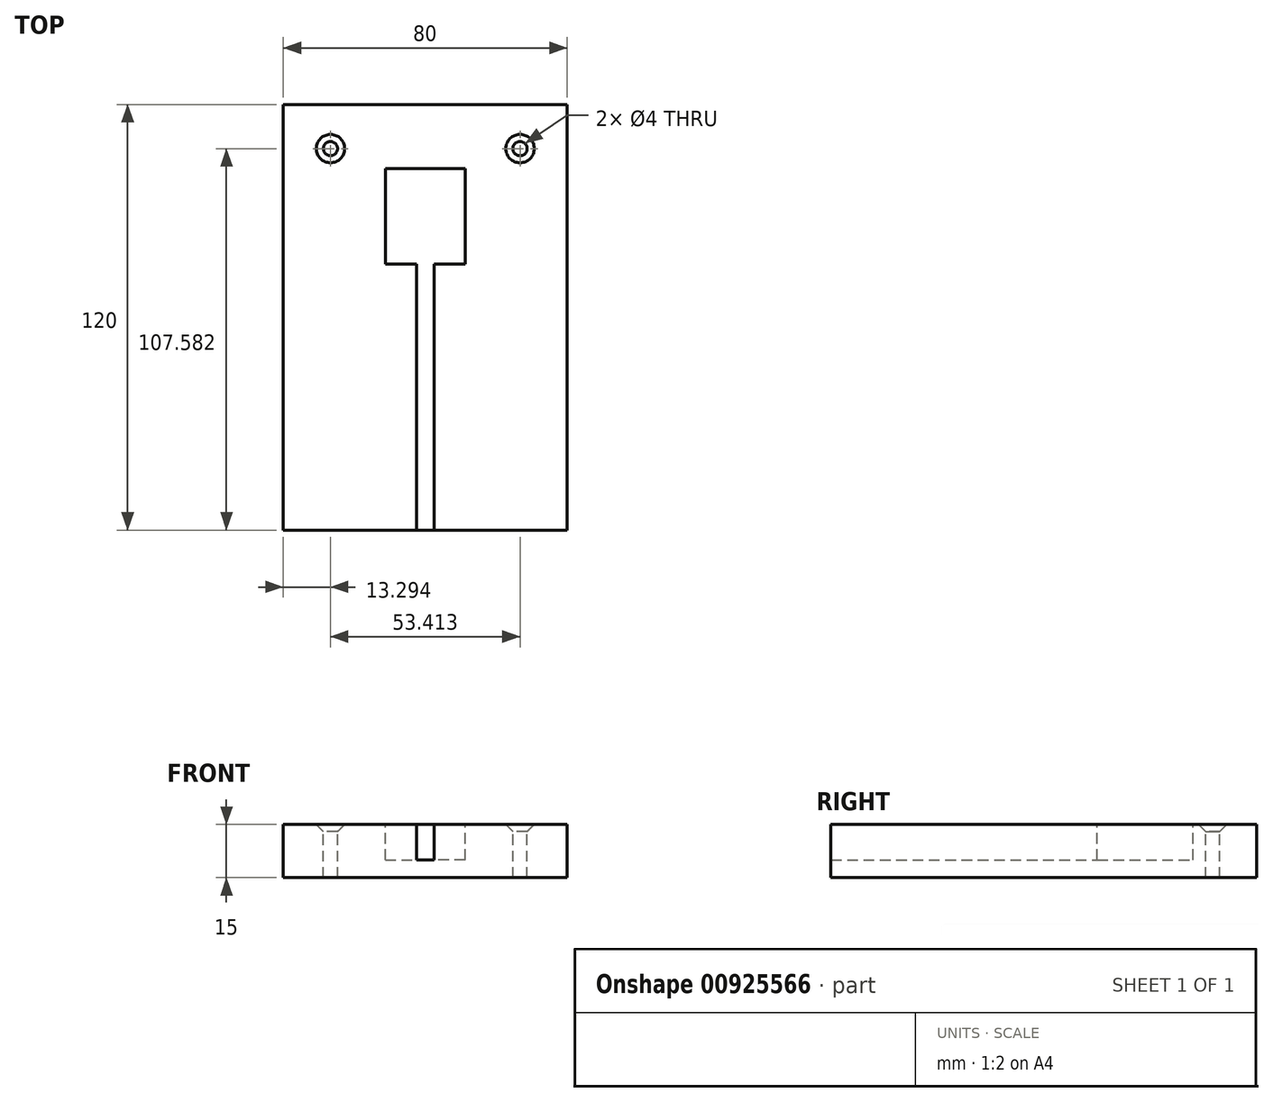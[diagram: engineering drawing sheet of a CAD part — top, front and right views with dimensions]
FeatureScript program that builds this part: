
annotation { "Feature Type Name" : "Feature", "Feature Type Description" : "" }
export const myFeature = defineFeature(function(context is Context, id is Id, definition is map)
    precondition{}
    {
        {
            var Q0;
            Q0=qCreatedBy(makeId("Top.planeOp"),FACE);
            var sketch = newSketch(context, id + "F0", { "sketchPlane" : qUnion([Q0])});
            skLineSegment(sketch, "E0.bottom", {"start": v(-40, 60) * mm, "end": v(40, 60) * mm});
            skLineSegment(sketch, "E0.top", {"start": v(-40, -60) * mm, "end": v(40, -60) * mm});
            skLineSegment(sketch, "E0.left", {"start": v(-40, 60) * mm, "end": v(-40, -60) * mm});
            skLineSegment(sketch, "E0.right", {"start": v(40, 60) * mm, "end": v(40, -60) * mm});
            skPoint(sketch, "E0.middle", {"position": v(0, 0) * mm});
            skSolve(sketch);
        }
        {
            var Q0;
            Q0 = qSketchRegion(id + "F0", true);
            extrude(context, id + "F1", {"entities" : qUnion([Q0]), "depth" : 15 * mm, "offsetDistance" : 25 * mm});
        }
        {
            var Q0;
            Q0=makeQuery(id+"F1.opExtrude","CAP_FACE",FACE,{"disambiguationData":[OSD([sQuery(id+"F0.wireOp",EDGE,"E0.bottom"),sQuery(id+"F0.wireOp",EDGE,"E0.top"),sQuery(id+"F0.wireOp",EDGE,"E0.left"),sQuery(id+"F0.wireOp",EDGE,"E0.right")])],"isStart":false});
            var sketch = newSketch(context, id + "F2", { "sketchPlane" : qUnion([Q0])});
            skLineSegment(sketch, "E1", {"start": v(-2.5, 15) * mm, "end": v(-11.26, 15) * mm});
            skLineSegment(sketch, "E2", {"start": v(-11.26, 15) * mm, "end": v(-11.26, 42) * mm});
            skLineSegment(sketch, "E3", {"start": v(0, -60) * mm, "end": v(-2.5, -60) * mm});
            skLineSegment(sketch, "E4", {"start": v(-2.5, -60) * mm, "end": v(-2.5, 15) * mm});
            skLineSegment(sketch, "E5.MirrorCS", {"start": v(2.5, -60) * mm, "end": v(2.5, 15) * mm});
            skPoint(sketch, "E6.end.orphan", {"position": v(0, 15) * mm});
            skPoint(sketch, "E7.end.orphan", {"position": v(6.37, 15) * mm});
            skPoint(sketch, "E8.start.orphan", {"position": v(0, 42) * mm});
            skPoint(sketch, "E9.end.orphan", {"position": v(12.75, 15) * mm});
            skLineSegment(sketch, "E10", {"start": v(0, 60) * mm, "end": v(0, 50.46) * mm});
            skLineSegment(sketch, "E11.MirrorCS", {"start": v(11.26, 15) * mm, "end": v(11.26, 42) * mm});
            skLineSegment(sketch, "E12", {"start": v(-11.26, 42) * mm, "end": v(11.26, 42) * mm});
            skLineSegment(sketch, "E13", {"start": v(11.26, 15) * mm, "end": v(2.5, 15) * mm});
            skSolve(sketch);
        }
        {
            var Q0;
            Q0 = qSketchRegion(id + "F2", true);
            var Q1;
            Q1=makeQuery(id+"F2.imprint","IMPRINT",FACE,{"disambiguationData":[TD([[makeQuery(id+"F2.imprint","IMPRINT",EDGE,{"derivedFrom":sQuery(id+"F2.wireOp",EDGE,"E1")}),-1.0]])]});
            extrude(context, id + "F3", {"entities" : qUnion([Q0, Q1]), "operationType" : NewBodyOperationType.REMOVE, "oppositeDirection" : true, "depth" : 10 * mm, "offsetDistance" : 25 * mm});
        }
        {
            var Q0;
            Q0=makeQuery(id+"F1.opExtrude","CAP_FACE",FACE,{"disambiguationData":[OSD([sQuery(id+"F0.wireOp",EDGE,"E0.bottom"),sQuery(id+"F0.wireOp",EDGE,"E0.top"),sQuery(id+"F0.wireOp",EDGE,"E0.left"),sQuery(id+"F0.wireOp",EDGE,"E0.right")])],"isStart":false});
            var sketch = newSketch(context, id + "F4", { "sketchPlane" : qUnion([Q0])});
            skPoint(sketch, "E14", {"position": v(-26.7, 47.58) * mm});
            skLineSegment(sketch, "E15", {"start": v(0, 60) * mm, "end": v(0, 49.68) * mm});
            skPoint(sketch, "E16.MirrorP", {"position": v(26.7, 47.58) * mm});
            skSolve(sketch);
        }
        {
            var Q0;
            Q0=sQuery(id+"F4.wireOp",VERTEX,"E14");
            var Q1;
            Q1=sQuery(id+"F4.wireOp",VERTEX,"E16.MirrorP");
            var Q2;
            Q2=makeQuery(id+"F1.opExtrude","SWEPT_BODY",BODY,{"disambiguationData":[OSD([sQuery(id+"F0.wireOp",EDGE,"E0.bottom"),sQuery(id+"F0.wireOp",EDGE,"E0.top"),sQuery(id+"F0.wireOp",EDGE,"E0.left"),sQuery(id+"F0.wireOp",EDGE,"E0.right")])]});
            hole(context, id + "F5", {"style" : HoleStyle.C_SINK, "endStyle" : HoleEndStyle.THROUGH, "standardTappedOrClearance" : lookupTablePath({ "standard" : "ISO", "size" : "4", "type" : "Drilled" }), "standardBlindInLast" : lookupTablePath({ "standard" : "ISO", "size" : "4", "type" : "Drilled" }), "holeDiameter" : 4 * mm, "cSinkDiameter" : 8 * mm, "cSinkAngle" : 90 * degree, "majorDiameter" : 5 * mm, "isTappedThrough" : true, "tappedDepth" : 12 * mm, "tapClearance" : 3, "locations" : qUnion([Q0, Q1]), "scope" : qUnion([Q2])});
        }
    });
